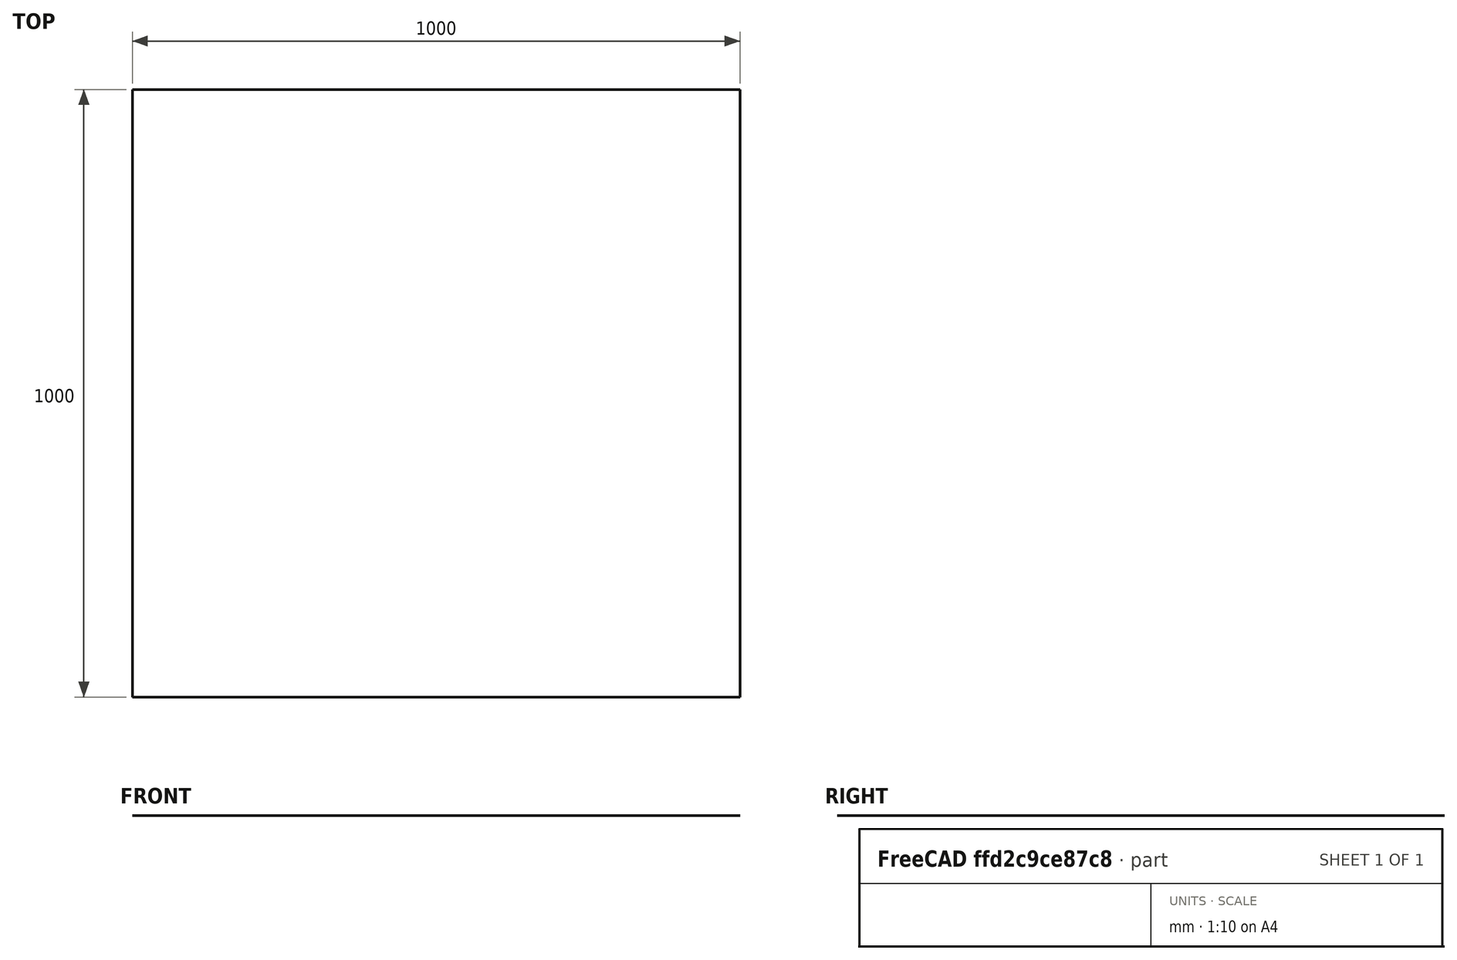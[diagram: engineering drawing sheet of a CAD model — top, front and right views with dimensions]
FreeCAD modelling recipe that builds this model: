
FCSTD DOCUMENT  (FreeCAD 0.19R)
Label: test_ifc_surface
License: All rights reserved
LicenseURL: http://en.wikipedia.org/wiki/All_rights_reserved
objects: Part::Part2DObjectPython×1, App::MaterialObjectPython×1, Part::FeaturePython×1, App::DocumentObjectGroupPython×1
note: 2 computed .brp shape members not serialized (recipe doc carries the construction recipe); baked Part::Feature solids carry a one-line shape summary decoded from their .brp

FEATURE [Part::Part2DObjectPython] Wire  # Draft 2D object (typed FeaturePython)
  Area = 1e+06
  ChamferSize = 0
  Closed = true
  End = (0,1000,0)
  FilletRadius = 0
  Length = 4000
  MakeFace = true
  Points = (4) [(0,0,0),(1000,0,0),(1000,1000,0),(0,1000,0)]
  Start = (0,0,0)
  Subdivisions = 0
FEATURE [App::MaterialObjectPython] Material  label="C25"  # material (typed FeaturePython)
  Description = A standard C-25 construction concrete
  Material = AuthorAndLicense=Concrete-Generic,CardName=Concrete-Generic,Color=(0.8, 0.8, 0.8, 1.0),CompressiveStrength=25 MPa,Density=2400 kg/m^3,+11 more (map truncated)
  ProductURL = https://en.wikipedia.org/wiki/Concrete
  StandardCode = Masterformat 03 33 13
  Transparency = 0
FEATURE [Part::FeaturePython] Component  label="IFCFace"  # Arch/BIM 148 (typed FeaturePython)
  Base = -> Wire
  HorizontalArea = 0
  IfcData = attributes={"GlobalId": {"name": "GlobalId", "type": "IfcGloballyUniqueId", "is_enum": false, "enum_values": []}, "Description": {"... (+605 chars omitted),+1 more (map truncated)
  IfcType = 148
  Material = -> Material
  MoveBase = false
  MoveWithHost = false
  PerimeterLength = 0
  PredefinedType = 2
  Thickness = 200
  VerticalArea = 0
FEATURE [App::DocumentObjectGroupPython] MaterialContainer  label="Materials"  # scripted group (container) (typed FeaturePython)
  Group = -> [Material]
